# Revit family: Power_Supply-Lutron-QS_DIN
name_source: partatom
category: Lighting Devices
revit_build: Autodesk Revit 2017 (Build: 20160720_1515(x64)
units: mm (PartAtom-declared; Revit-internal decimal feet)

## family parameters
Cut with Voids When Loaded = No
Host = Face
Maintain Annotation Orientation = Yes
OmniClass Number = 23.80.30.11
OmniClass Title = Power Supply Devices
Part Type = Normal
Room Calculation Point = No
Round Connector Dimension = Use Radius
Shared = No

## types (1)
- QSPS-DH-1-75-H
    Assembly Code = D3060800
    Cost = 0 $
    Cover Height = 0' - 1 25/32"
    Default Elevation = 4' - 0"
    Description = DIN Rail Mount Power Supply with Wire Harnesses
    Enclosure Depth = 0' - 1 31/32"
    Frequency = 50/60 Hz
    Input Voltage Range = 100 V - 277 V
    Instruction Sheet Link = http://www.lutron.com
    Label = PS
    Load Classification = Power
    Manufacturer = Lutron Electronics Co., Inc
    Manufacturer Fax Number = 610-282-1243
    Material = Plastic - Lutron - Grey
    Maximum Operating Temperature = 131 °F
    Minimum Operating Temperature = 32 °F
    Model = QSPS-DH-1-75-H
    Number of Poles = 1
    Output Current = 3 A
    Output Power = 60 VA
    Output Voltage = 24 V
    Overall Depth = 0' - 2 13/32"
    Overall Height = 0' - 3 17/32"
    Overall Width = 0' - 3 17/32"
    Performance URL = http://www.lutron.com
    Product Documentation Link = http://www.lutron.com
    Product Name = DIN Rail Mount Power Supply with Wire Harnesses
    Product Page URL = http://www.lutron.com
    Rail Mount Offset = 0' - 2 5/32"
    Series = HomeWorks QS
    URL = http://www.lutron.com
    Version = 2017 - v1.0b
    Video Link = https://www.youtube.com
    Warranty URL = http://www.lutron.com

## geometry (parser evidence)
native form markers: Sweep x4
no freeform markers — native parametric forms only
